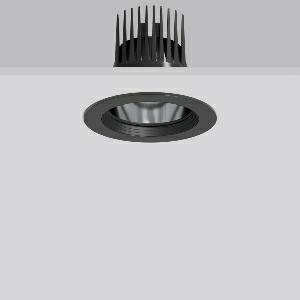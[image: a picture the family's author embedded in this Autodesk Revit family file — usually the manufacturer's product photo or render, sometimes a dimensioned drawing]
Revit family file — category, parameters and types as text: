
# Revit family: heledon_maxi_e_901772_003_9dd5
name_source: partatom
category: Lighting Fixtures
units: mm (PartAtom-declared; Revit-internal decimal feet)

## family parameters
Cut with Voids When Loaded = No
Host = Face
Light Source = No
Part Type = Normal
Room Calculation Point = No
Round Connector Dimension = Use Diameter
Shared = No

## types (1)
- HELEDON maxi E (1 x LED Modul 932 fresh meat, 2150 lm, 3200)
    Apparent Load = 33 VA
    Approval mark = CE
    CIE Flux Codes = 100 100 100 100 100
    Color Rendering = 90
    Color Temperature = 3200
    Default Elevation = 1800 mm
    Description = Series: HELEDON maxi
Round recessed downlight. Housing: die-cast aluminium, powder-coated. Black plastic ring and recessed LED to prevent glare from the side. Optical assembly with reflector made of MIRO-Silver with 98% total light reflection for outstanding efficiency - can be changed without tools. Special LED for illumination of meat included. Suitable for Recessed ceiling mounting. Installation without tools thanks to spring fastening system. Including separate LED converter with connecting cable 600 mm.High quality converter without flickering and stroboscopic effect. Through-wiring box (5 pole) available as accessory. The following accessories can be mounted without use of tools: interchangeable lenses, decorative glasses, honeycomb louvre, clear and frosted diffusers, white interchangeable plastic ring. 
Colour: deep black, matt (RAL 9005)
Diameter: 162 mm
Height: 3 mm
Cut-out diameter: 152 mm
Recess height: 200 mm
Luminaire: recess height: 135 mm
Lamp: LED
Socket: without socket
Colour temperature: fresh meat
System power: 33 W
Rated luminous flux: 2150 lm
Luminous efficiency: 65 lm/W
Control gear: Regulated power supply
Protection class: II
Type of protection: IP 20
    Height = 0 mm  [stored 0 ft]
    Lamp = 1 x LED Modul 932 fresh meat
    Lamp Light Flux = 2150 lm
    Lamp count = 1
    Length = 162 mm
    Lifetime = 50000 h
    Luminous efficacy = 65 lm/W
    Manufacturer = RZB
    ModVariant = No
    Model = 901772.003
    Mounting Place = Ceiling
    Mounting Type = Recessed
    Number of Poles = 1
    OnlyDefault = Yes
    Power Factor = 1
    Product Name = HELEDON maxi E
    Product group = Recessed downlights
    ProductGroupID = 402
    Protection Class = Protection class II
    Protection Degree = IP 20
    RLX_Detail_Level = 1
    RLX_Emergency_Light_Flux = 0 lm
    RLX_Emergency_Type = 0
    RLX_Emergency_Type_DB = No
    RlxData = <blob elided: 121597 chars, md5=664e4ad5>
    Socket = socket
    Standby Power = 0 W
    System Light Flux = 2150 lm
    System Power = 33 W
    Type Comments = Product without accessories
    Type Image = 901662.003.jpg
    URL = http://relux.com
    VarID = ---
    Voltage = 230 V
    Voltage Range = 220-240 V
    Weight = 0.00 kg
    Width = 0 mm  [stored 0 ft]

note: [stored X ft] marks values corroborated as IEEE doubles in the binary element streams (Revit-internal decimal feet)

## geometry (parser evidence)
native form markers: Blend x4, Sweep x13
no freeform markers — native parametric forms only
